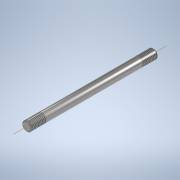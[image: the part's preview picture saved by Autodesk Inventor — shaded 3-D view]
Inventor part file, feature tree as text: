
AUTODESK INVENTOR PART (.ipt)
format: ipt  version: 2021.1 (Build 251245000, 245)  size: 111,616 bytes
history: native  units: in
note: dims shown in document units (in); Inventor stores cm internally (conversion verified against a paired STEP export)
features: thread x2, extrude x1, chamfer x1, sketch x1
ambient origin geometry x8: Origin, YZ Plane, XZ Plane, XY Plane, X Axis, Y Axis, Z Axis, Center Point
bodies: Solid1 (feature_tree)
feature tree (5):
  extrude  "Extrusion1"  Depth=8.2in TaperAngle=0.0deg
  thread  "Thread1"  [1 undecoded]
  thread  "Thread2"  [1 undecoded]
  chamfer  "Chamfer1"  Distance=0.05in Angle=45.0deg
  sketch  "Sketch1"  dims[d0=0.6in d1=8.2in d2=0.0in d3=1.0in d4=0.0in d5=1.0in d6=0.0in d7=0.05in d8=0.125in d9=45.0deg]
note: 2 required parameter values undecoded (feature->parameter linkage not recoverable at this tier; creation-order binding heuristic only, values carry confidence <= 0.55)
